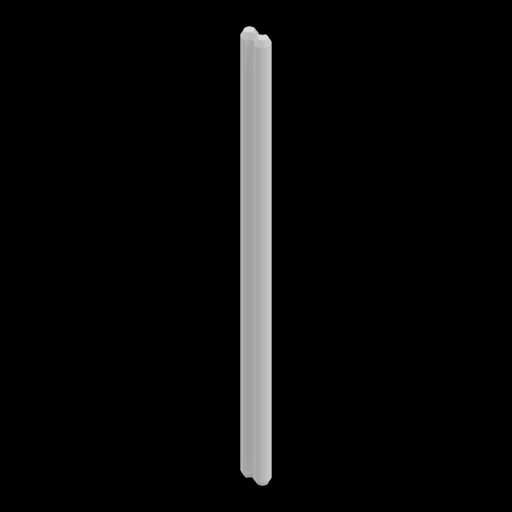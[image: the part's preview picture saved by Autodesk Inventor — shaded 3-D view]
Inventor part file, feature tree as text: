
AUTODESK INVENTOR PART (.ipt)
format: ipt  version: 2023 (Build 270158000, 158)  size: 129,024 bytes
history: native  units: mm
features: chamfer x8, extrude x1, sketch x1
ambient origin geometry x8: Origin, YZ Plane, XZ Plane, XY Plane, X Axis, Y Axis, Z Axis, Center Point
bodies: Solid1 (feature_tree)
feature tree (10):
  extrude  "Extrusion1"  Depth=11.0mm
  chamfer  "Chamfer1"  Distance=15.0mm
  chamfer  "Chamfer2"  Distance=15.0mm
  chamfer  "Chamfer3"  Distance=6.5mm
  chamfer  "Chamfer4"  Distance=325.0mm
  chamfer  "Chamfer5"  Distance=2.0mm Angle=30.0deg
  chamfer  "Chamfer6"  Distance=2.0mm Angle=30.0deg
  chamfer  "Chamfer7"  Distance=2.0mm Angle=30.0deg
  chamfer  "Chamfer8"  Distance=2.0mm Angle=30.0deg
  sketch  "Sketch1"  dims[d0=11.0mm d1=11.0mm d2=15.0mm d3=15.0mm d4=6.5mm d5=325.0mm d6=0.0mm d7=2.0mm d8=4.0mm d9=30.0deg d10=2.0mm d11=4.0mm d12=30.0deg d13=2.0mm d14=4.0mm d15=30.0deg d16=2.0mm d17=4.0mm d18=30.0deg d19=2.0mm d20=4.0mm d21=30.0deg d22=4.0mm d23=2.0mm d24=30.0deg d25=4.0mm d26=2.0mm d27=30.0deg d28=4.0mm d29=2.0mm d30=30.0deg]
